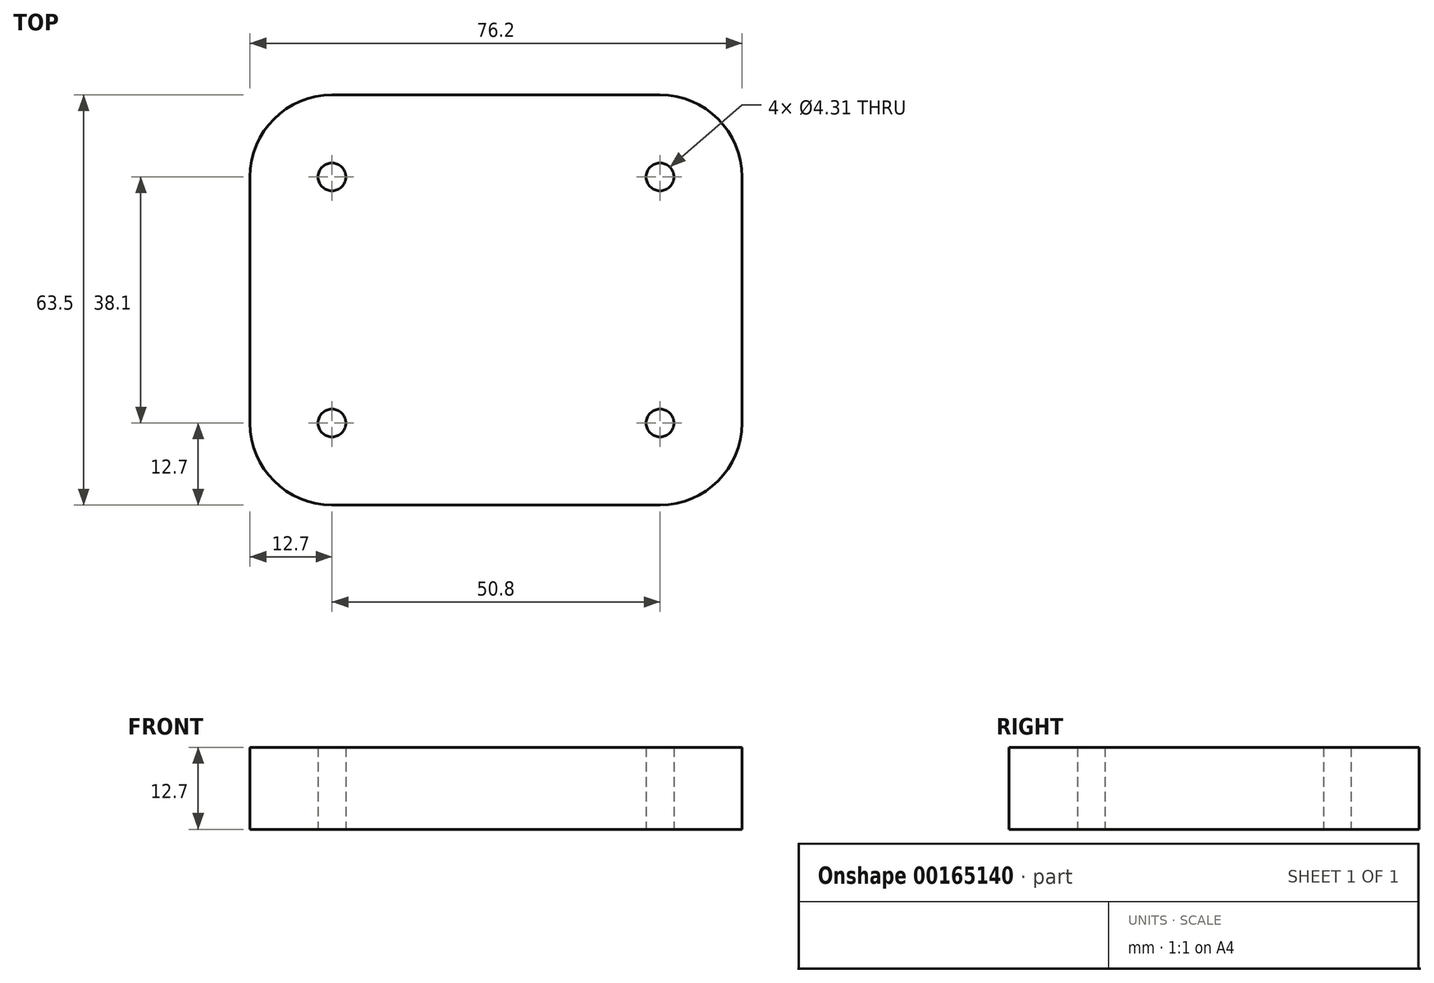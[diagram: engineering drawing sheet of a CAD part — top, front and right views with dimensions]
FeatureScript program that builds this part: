
annotation { "Feature Type Name" : "Feature", "Feature Type Description" : "" }
export const myFeature = defineFeature(function(context is Context, id is Id, definition is map)
    precondition{}
    {
        {
            var Q0;
            Q0=qCreatedBy(makeId("Top.planeOp"),FACE);
            var sketch = newSketch(context, id + "F0", { "sketchPlane" : qUnion([Q0])});
            skLineSegment(sketch, "E0.bottom", {"start": v(25.4, 19.05) * mm, "end": v(-25.4, 19.05) * mm, "construction": true});
            skLineSegment(sketch, "E0.top", {"start": v(25.4, -19.05) * mm, "end": v(-25.4, -19.05) * mm, "construction": true});
            skLineSegment(sketch, "E0.left", {"start": v(25.4, 19.05) * mm, "end": v(25.4, -19.05) * mm, "construction": true});
            skLineSegment(sketch, "E0.right", {"start": v(-25.4, 19.05) * mm, "end": v(-25.4, -19.05) * mm, "construction": true});
            skPoint(sketch, "E0.middle", {"position": v(0, 0) * mm});
            skLineSegment(sketch, "E1.bottom", {"start": v(38.1, -31.75) * mm, "end": v(-38.1, -31.75) * mm});
            skLineSegment(sketch, "E1.top", {"start": v(38.1, 31.75) * mm, "end": v(-38.1, 31.75) * mm});
            skLineSegment(sketch, "E1.left", {"start": v(38.1, -31.75) * mm, "end": v(38.1, 31.75) * mm});
            skLineSegment(sketch, "E1.right", {"start": v(-38.1, -31.75) * mm, "end": v(-38.1, 31.75) * mm});
            skLineSegment(sketch, "E2", {"start": v(25.4, -19.05) * mm, "end": v(25.4, -31.75) * mm, "construction": true});
            skLineSegment(sketch, "E3", {"start": v(25.4, -19.05) * mm, "end": v(38.1, -19.05) * mm, "construction": true});
            skCircle(sketch, "E4", {"center": v(-25.4, -19.05) * mm, "radius": 2.15 * mm});
            skCircle(sketch, "E5", {"center": v(-25.4, 19.05) * mm, "radius": 2.15 * mm});
            skCircle(sketch, "E6", {"center": v(25.4, -19.05) * mm, "radius": 2.15 * mm});
            skCircle(sketch, "E7", {"center": v(25.4, 19.05) * mm, "radius": 2.15 * mm});
            skSolve(sketch);
        }
        {
            var Q0;
            Q0 = qSketchRegion(id + "F0", true);
            extrude(context, id + "F1", {"entities" : qUnion([Q0]), "depth" : 12.7 * mm});
        }
        {
            var Q0;
            Q0=makeQuery(id+"F1.opExtrude","SWEPT_EDGE",EDGE,{"disambiguationData":[OSD([sQuery(id+"F0.wireOp",EDGE,"E1.bottom"),sQuery(id+"F0.wireOp",EDGE,"E1.right")])]});
            var Q1;
            Q1=makeQuery(id+"F1.opExtrude","SWEPT_EDGE",EDGE,{"disambiguationData":[OSD([sQuery(id+"F0.wireOp",EDGE,"E1.bottom"),sQuery(id+"F0.wireOp",EDGE,"E1.left")])]});
            var Q2;
            Q2=makeQuery(id+"F1.opExtrude","SWEPT_EDGE",EDGE,{"disambiguationData":[OSD([sQuery(id+"F0.wireOp",EDGE,"E1.top"),sQuery(id+"F0.wireOp",EDGE,"E1.left")])]});
            var Q3;
            Q3=makeQuery(id+"F1.opExtrude","SWEPT_EDGE",EDGE,{"disambiguationData":[OSD([sQuery(id+"F0.wireOp",EDGE,"E1.top"),sQuery(id+"F0.wireOp",EDGE,"E1.right")])]});
            fillet(context, id + "F2", {"entities" : qUnion([Q0, Q1, Q2, Q3]), "radius" : 12.7 * mm, "tangentPropagation" : true, "allowEdgeOverflow" : false});
        }
    });
